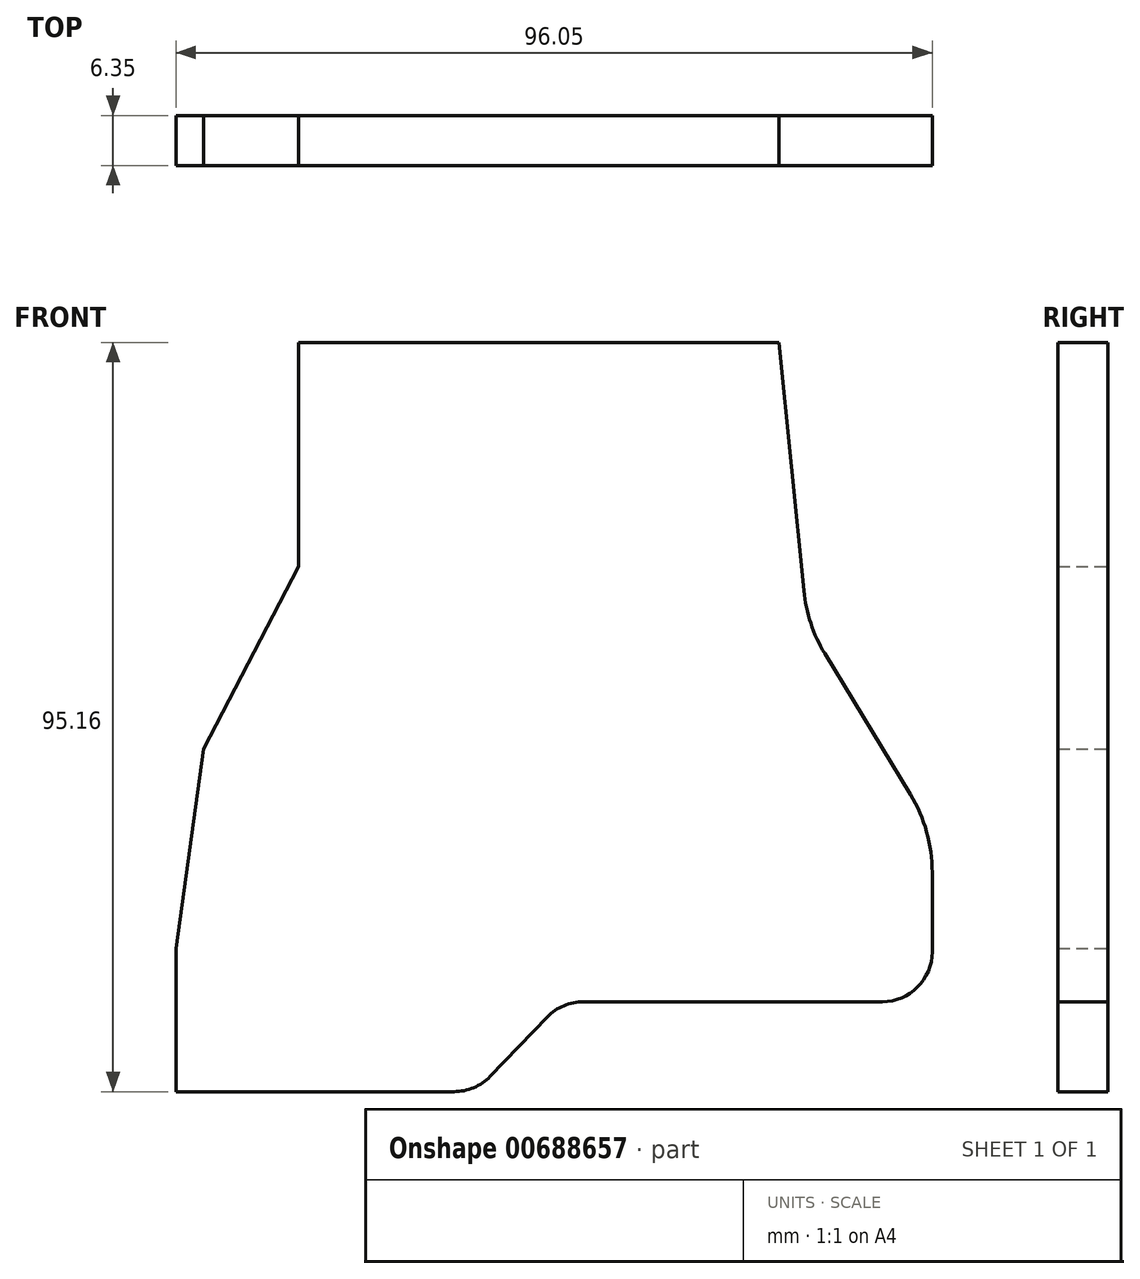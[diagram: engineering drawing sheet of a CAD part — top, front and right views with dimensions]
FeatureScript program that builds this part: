
annotation { "Feature Type Name" : "Feature", "Feature Type Description" : "" }
export const myFeature = defineFeature(function(context is Context, id is Id, definition is map)
    precondition{}
    {
        {
            var Q0;
            Q0=qCreatedBy(makeId("Front.planeOp"),FACE);
            var sketch = newSketch(context, id + "F0", { "sketchPlane" : qUnion([Q0])});
            skLineSegment(sketch, "E0", {"start": v(21.33, 0) * mm, "end": v(56.65, 0) * mm});
            skLineSegment(sketch, "E1", {"start": v(61.23, 1.94) * mm, "end": v(68.5, 9.49) * mm});
            skLineSegment(sketch, "E2", {"start": v(73.07, 11.43) * mm, "end": v(111.03, 11.43) * mm});
            skLineSegment(sketch, "E3", {"start": v(117.38, 17.78) * mm, "end": v(117.38, 27.85) * mm});
            skPoint(sketch, "E4.visualSharp", {"position": v(70.37, 11.43) * mm});
            skArc(sketch, "E4.filletArc", {"start": v(73.07, 11.43) * mm, "mid": v(70.58, 10.92) * mm, "end": v(68.5, 9.49) * mm});
            skPoint(sketch, "E5.visualSharp", {"position": v(59.35, 0) * mm});
            skArc(sketch, "E5.filletArc", {"start": v(56.65, 0) * mm, "mid": v(59.14, 0.5) * mm, "end": v(61.23, 1.94) * mm});
            skPoint(sketch, "E6.visualSharp", {"position": v(117.38, 11.43) * mm});
            skArc(sketch, "E6.filletArc", {"start": v(111.03, 11.43) * mm, "mid": v(115.52, 13.29) * mm, "end": v(117.38, 17.78) * mm});
            skLineSegment(sketch, "E7", {"start": v(114.62, 37.74) * mm, "end": v(103.73, 55.66) * mm});
            skLineSegment(sketch, "E8", {"start": v(101.06, 63.65) * mm, "end": v(97.91, 95.16) * mm});
            skPoint(sketch, "E9.visualSharp", {"position": v(117.38, 33.18) * mm});
            skArc(sketch, "E9.filletArc", {"start": v(117.38, 27.85) * mm, "mid": v(116.68, 32.98) * mm, "end": v(114.62, 37.74) * mm});
            skPoint(sketch, "E10.visualSharp", {"position": v(101.5, 59.35) * mm});
            skArc(sketch, "E10.filletArc", {"start": v(101.06, 63.65) * mm, "mid": v(101.95, 59.5) * mm, "end": v(103.73, 55.66) * mm});
            skLineSegment(sketch, "E11", {"start": v(97.91, 95.16) * mm, "end": v(36.91, 95.16) * mm});
            skLineSegment(sketch, "E12", {"start": v(36.91, 95.16) * mm, "end": v(36.91, 66.7) * mm});
            skLineSegment(sketch, "E13", {"start": v(36.91, 66.7) * mm, "end": v(24.84, 43.53) * mm});
            skLineSegment(sketch, "E14", {"start": v(24.84, 43.53) * mm, "end": v(21.33, 18.21) * mm});
            skLineSegment(sketch, "E15", {"start": v(21.33, 18.21) * mm, "end": v(21.33, 0) * mm});
            skSolve(sketch);
        }
        {
            var Q0;
            Q0 = qSketchRegion(id + "F0", true);
            extrude(context, id + "F1", {"entities" : qUnion([Q0]), "depth" : 6.35 * mm, "offsetDistance" : 25.4 * mm});
        }
    });
